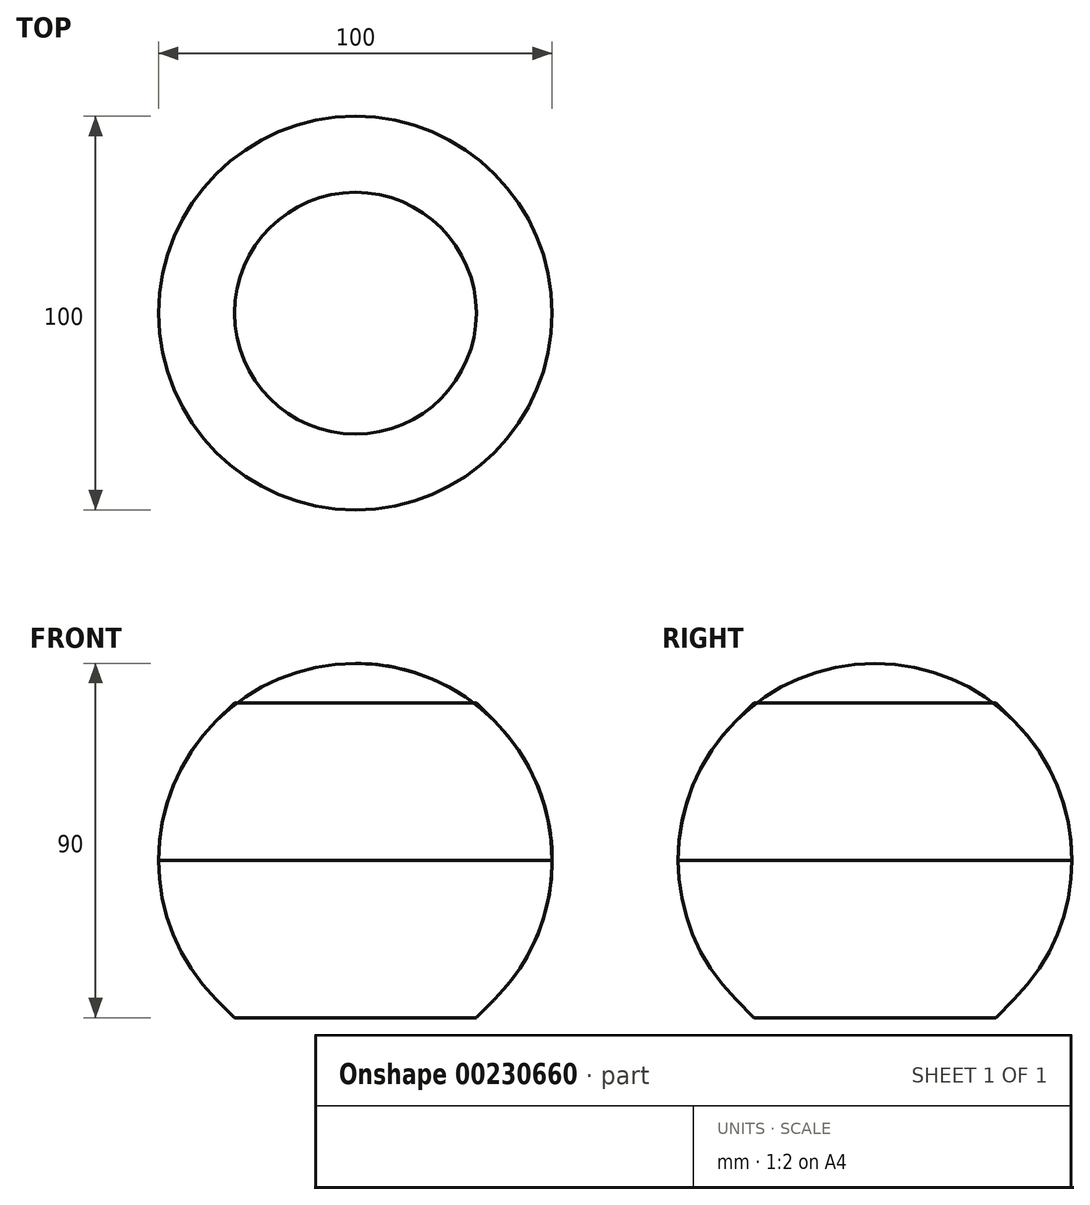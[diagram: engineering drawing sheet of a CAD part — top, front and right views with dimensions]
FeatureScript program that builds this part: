
annotation { "Feature Type Name" : "Feature", "Feature Type Description" : "" }
export const myFeature = defineFeature(function(context is Context, id is Id, definition is map)
    precondition{}
    {
        {
            var Q0;
            Q0=qCreatedBy(makeId("Front.planeOp"),FACE);
            var sketch = newSketch(context, id + "F0", { "sketchPlane" : qUnion([Q0])});
            skArc(sketch, "E0", {"start": v(50, 0) * mm, "mid": v(35.36, 35.36) * mm, "end": v(0, 50) * mm});
            skLineSegment(sketch, "E1", {"start": v(0, 50) * mm, "end": v(0, 0) * mm});
            skLineSegment(sketch, "E2", {"start": v(50, 0) * mm, "end": v(0, 0) * mm});
            skSolve(sketch);
        }
        {
            var Q0;
            Q0 = qSketchRegion(id + "F0", true);
            var Q1;
            Q1=sQuery(id+"F0.wireOp",EDGE,"E1");
            revolve(context, id + "F1", {"entities" : qUnion([Q0]), "axis" : qUnion([Q1]), "revolveType" : RevolveType.FULL});
        }
        {
            var Q0;
            Q0=qCreatedBy(makeId("Front.planeOp"),FACE);
            var sketch = newSketch(context, id + "F2", { "sketchPlane" : qUnion([Q0])});
            skArc(sketch, "E3", {"start": v(35.36, -35.36) * mm, "mid": v(50, 0) * mm, "end": v(35.36, 35.36) * mm});
            skLineSegment(sketch, "E4", {"start": v(35.36, -35.36) * mm, "end": v(30.71, -40) * mm});
            skLineSegment(sketch, "E5", {"start": v(30.71, -40) * mm, "end": v(0, -40) * mm});
            skLineSegment(sketch, "E6", {"start": v(35.36, 35.36) * mm, "end": v(30.71, 40) * mm});
            skLineSegment(sketch, "E7", {"start": v(30.71, 40) * mm, "end": v(0, 40) * mm});
            skLineSegment(sketch, "E8", {"start": v(0, 40) * mm, "end": v(0, -40) * mm});
            skSolve(sketch);
        }
        {
            var Q0;
            Q0 = qSketchRegion(id + "F2", true);
            var Q1;
            Q1=sQuery(id+"F2.wireOp",EDGE,"E8");
            revolve(context, id + "F3", {"entities" : qUnion([Q0]), "axis" : qUnion([Q1]), "revolveType" : RevolveType.FULL});
        }
    });
